# Revit family: Sanitary_Accessories_Johnson-Suisse_Cube_Double_Robe_Hook
name_source: partatom
category: Plumbing Fixtures
revit_build: Autodesk Revit 2015 (Build: 20140606_1530(x64)
units: mm (PartAtom-declared; Revit-internal decimal feet)

## types (1)
- Cube Double Robe Hook
    BIMobject category = Accessories
    Brand url = http://www.johnsonsuisse.com.au
    Design country = Spain
    EAN code = https://9325304004457
    Edition number = 1
    IFC Classification = Object
    Manufacturer country = China
    Manufacturer name = Johnson Suisse
    Material main = Metal
    Material secondary = Chrome
    NBS Reference Code = 35-75-18
    NBS Reference Description = Clothes Hooks
    Nominal height = 45 mm  [stored 0.147638 ft]
    Nominal width = 65 mm  [stored 0.213255 ft]
    Product Guid = 66c579aa-b8bd-43e2-8c7c-105d198d7417
    Product SKU = GDC160122
    Product data url = https://bimobject.com
    Product family = Cube
    Product group = Accessories
    Product url = https://johnsonsuisse.com.au
    QR code = http://bimobject.com
    Technical description = https://johnsonsuisse.com.au
    Type = cube_double_robe_hook : Default
    UNSPSC Code = 52171001
    Uniclass 1.4 Code = L824
    Uniclass 1.4 Description = Bathroom, toilet furniture and fittings
    Weight Net (Kg) = 0.196

note: [stored X ft] marks values corroborated as IEEE doubles in the binary element streams (Revit-internal decimal feet)

## geometry (parser evidence)
native form markers: Sweep x4
no freeform markers — native parametric forms only
